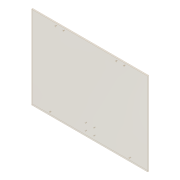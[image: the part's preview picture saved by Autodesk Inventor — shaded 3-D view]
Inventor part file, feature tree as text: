
AUTODESK INVENTOR PART (.ipt)
format: ipt  version: 2012 (Build 160160000, 160)  size: 98,816 bytes
history: native  units: in
note: dims shown in document units (in); Inventor stores cm internally (conversion verified against a paired STEP export)
features: hole x5, pattern_linear x3, extrude x1, sketch x1
ambient origin geometry x8: Origin, YZ Plane, XZ Plane, XY Plane, X Axis, Y Axis, Z Axis, Center Point
bodies: Solid1 (feature_tree)
feature tree (10):
  extrude  "Extrusion1"  Depth=31.5in
  hole  "Hole1"  [1 undecoded]
  pattern_linear  "Rectangular Pattern1"  Count1=2 Spacing1=2.625in
  hole  "Hole2"  [1 undecoded]
  pattern_linear  "Rectangular Pattern2"  Count1=2 Spacing1=3.0in
  hole  "Hole3"  [1 undecoded]
  pattern_linear  "Rectangular Pattern3"  [2 undecoded]
  hole  "Hole4"  [1 undecoded]
  hole  "Hole5"  [1 undecoded]
  sketch  "Sketch1"  dims[d0=44.0in d1=31.5in d2=0.5in d3=0.0in d4=20.4063in d5=1.625in d6=0.265in d7=0.75in d8=0.375in d9=0.25in d10=0.5635in d11=1.0in d12=0.8108in d13=0.7874in d15=2.625in d16=0.7874in d18=3.1875in d19=9.0in d20=1.125in d21=0.265in d22=0.75in d23=0.5in d24=0.25in d25=0.5635in d26=1.0in d27=0.8108in d28=0.7874in d30=3.0in d31=9.0in d32=1.125in d33=0.265in d34=0.75in d35=0.5in d36=0.25in d37=0.5635in d38=1.0in d39=0.8108in d40=0.7874in d42=3.0in d43=1.125in d44=6.875in d45=0.265in d46=0.75in d47=0.5in d48=0.25in d49=0.5635in d50=1.0in d51=0.8108in d52=6.875in d53=1.125in d54=0.265in d55=0.75in d56=0.5in d57=0.25in d58=0.5635in d59=1.0in d60=0.8108in]
note: 7 required parameter values undecoded (feature->parameter linkage not recoverable at this tier; creation-order binding heuristic only, values carry confidence <= 0.55)
